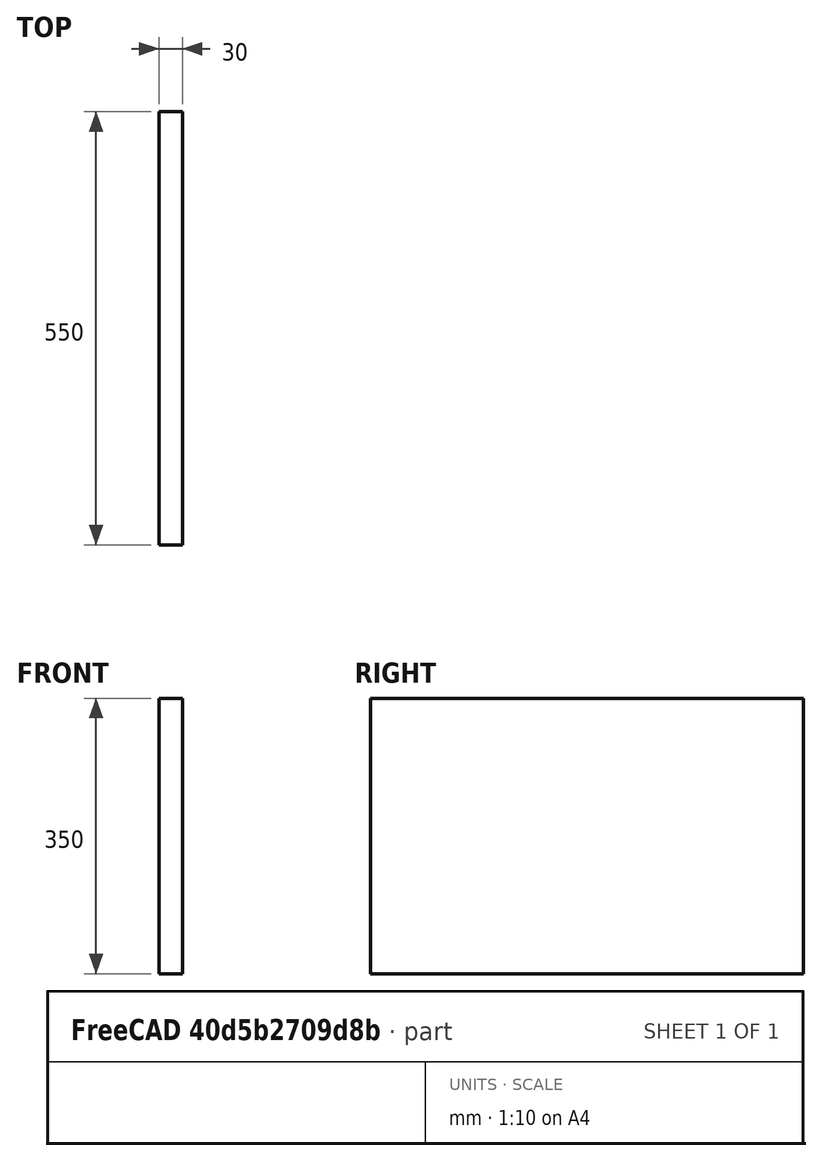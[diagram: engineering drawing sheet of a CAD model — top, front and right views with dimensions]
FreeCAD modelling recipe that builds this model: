
FCSTD DOCUMENT  (FreeCAD 1.0R39319 (Git))
Label: screen
License: All rights reserved
LicenseURL: http://en.wikipedia.org/wiki/All_rights_reserved
objects: Sketcher::SketchObject×1, PartDesign::Pad×1, PartDesign::Body×1
note: 6 computed .brp shape members not serialized (recipe doc carries the construction recipe); baked Part::Feature solids carry a one-line shape summary decoded from their .brp

FEATURE [Sketcher::SketchObject] Sketch
  ArcFitTolerance = 0
  AttachmentSupport = -> [YZ_Plane]
  FullyConstrained = false
  MakeInternals = false
  MapMode = 5
  Placement = pos=(0,0,0) rot=(0.57735,0.57735,0.57735;2.0944rad)
  sketch-geometry (4):
    g0: LineSegment StartX=0 StartY=0 StartZ=0 EndX=550 EndY=0 EndZ=0
    g1: LineSegment StartX=550 StartY=0 StartZ=0 EndX=550 EndY=350 EndZ=0
    g2: LineSegment StartX=550 StartY=350 StartZ=0 EndX=0 EndY=350 EndZ=0
    g3: LineSegment StartX=0 StartY=350 StartZ=0 EndX=0 EndY=0 EndZ=0
  constraints (11):
    c: Coincident(g0,g1)
    c: Coincident(g1,g2)
    c: Coincident(g2,g3)
    c: Coincident(g3,g0)
    c: Horizontal(g0)
    c: Horizontal(g2)
    c: Vertical(g1)
    c: Vertical(g3)
    c: Coincident(g0,g-1)
    c: DistanceX(g0,g0) = 550
    c: DistanceY(g3,g3) = 350
FEATURE [PartDesign::Pad] Pad
  AllowMultiFace = false
  Direction = (1,1,1)
  Length = 30
  Length2 = 100
  Placement = pos=(0,0,0) rot=(0.57735,0.57735,0.57735;2.0944rad)
  Profile = -> Sketch
  Suppressed = false
  Type = 0
FEATURE [PartDesign::Body] Body
  AllowCompound = false
  Group = -> [Sketch,Pad]
  Origin = -> Origin
  Tip = -> Pad
